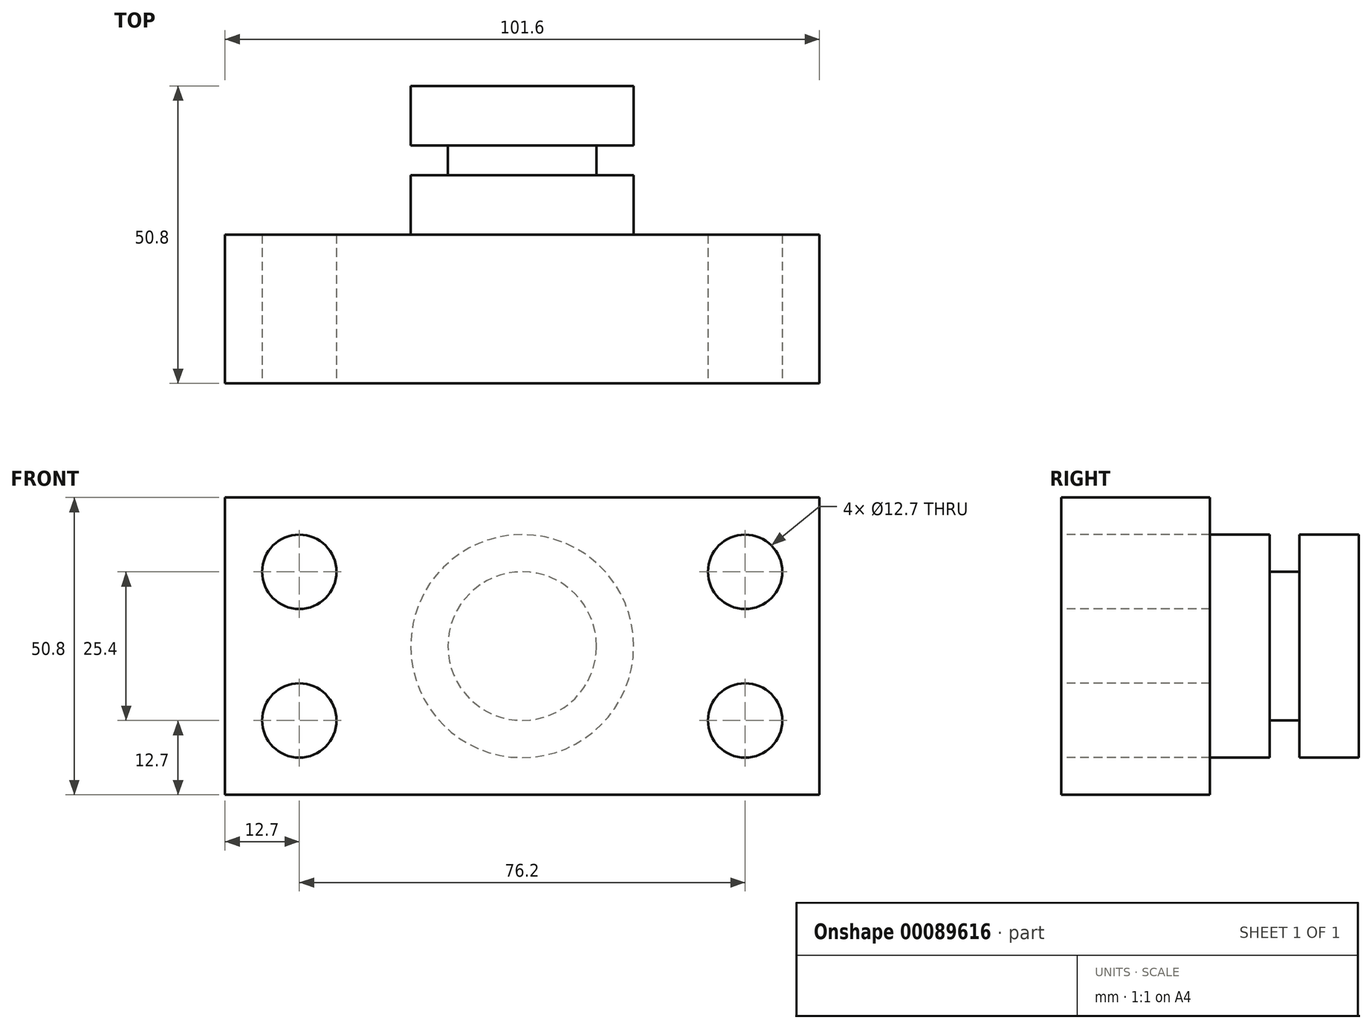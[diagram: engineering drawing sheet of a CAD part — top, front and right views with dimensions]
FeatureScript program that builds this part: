
annotation { "Feature Type Name" : "Feature", "Feature Type Description" : "" }
export const myFeature = defineFeature(function(context is Context, id is Id, definition is map)
    precondition{}
    {
        {
            var Q0;
            Q0=qCreatedBy(makeId("Front.planeOp"),FACE);
            var sketch = newSketch(context, id + "F0", { "sketchPlane" : qUnion([Q0])});
            skLineSegment(sketch, "E0", {"start": v(-50.8, 25.4) * mm, "end": v(50.8, 25.4) * mm});
            skLineSegment(sketch, "E1", {"start": v(50.8, 25.4) * mm, "end": v(50.8, -25.4) * mm});
            skLineSegment(sketch, "E2", {"start": v(50.8, -25.4) * mm, "end": v(-50.8, -25.4) * mm});
            skLineSegment(sketch, "E3", {"start": v(-50.8, -25.4) * mm, "end": v(-50.8, 25.4) * mm});
            skSolve(sketch);
        }
        {
            var Q0;
            Q0=makeQuery(id+"F0.imprint","IMPRINT",FACE,{"disambiguationData":[TD([[makeQuery(id+"F0.imprint","IMPRINT",EDGE,{"derivedFrom":sQuery(id+"F0.wireOp",EDGE,"E0")}),-1.0]])]});
            extrude(context, id + "F1", {"entities" : qUnion([Q0]), "depth" : 25.4 * mm});
        }
        {
            var Q0;
            Q0=makeQuery(id+"F1.opExtrude","CAP_FACE",FACE,{"disambiguationData":[OSD([sQuery(id+"F0.wireOp",EDGE,"E0"),sQuery(id+"F0.wireOp",EDGE,"E1"),sQuery(id+"F0.wireOp",EDGE,"E2"),sQuery(id+"F0.wireOp",EDGE,"E3")])],"isStart":false});
            var sketch = newSketch(context, id + "F2", { "sketchPlane" : qUnion([Q0])});
            skCircle(sketch, "E4", {"center": v(-38.1, 12.7) * mm, "radius": 6.35 * mm});
            skCircle(sketch, "E5", {"center": v(-38.1, -12.7) * mm, "radius": 6.35 * mm});
            skLineSegment(sketch, "E6", {"start": v(0, 34.69) * mm, "end": v(0, -31.44) * mm, "construction": true});
            skPoint(sketch, "E6.endSnap0", {"position": v(0, -25.4) * mm});
            skCircle(sketch, "E7.MirrorC", {"center": v(38.1, -12.7) * mm, "radius": 6.35 * mm});
            skCircle(sketch, "E8.MirrorC", {"center": v(38.1, 12.7) * mm, "radius": 6.35 * mm});
            skSolve(sketch);
        }
        {
            var Q0;
            Q0 = qSketchRegion(id + "F2", true);
            extrude(context, id + "F3", {"entities" : qUnion([Q0]), "operationType" : NewBodyOperationType.REMOVE, "endBound" : BoundingType.THROUGH_ALL, "oppositeDirection" : true, "depth" : 25.4 * mm});
        }
        {
            var Q0;
            Q0=qCreatedBy(makeId("Top.planeOp"),FACE);
            var sketch = newSketch(context, id + "F4", { "sketchPlane" : qUnion([Q0])});
            skLineSegment(sketch, "E9", {"start": v(-19.05, 0) * mm, "end": v(0, 0) * mm});
            skLineSegment(sketch, "E10", {"start": v(0, 0) * mm, "end": v(0, 25.4) * mm});
            skLineSegment(sketch, "E11", {"start": v(0, 25.4) * mm, "end": v(-19.05, 25.4) * mm});
            skLineSegment(sketch, "E12", {"start": v(-19.05, 25.4) * mm, "end": v(-19.05, 0) * mm});
            skLineSegment(sketch, "E13", {"start": v(0, 50.58) * mm, "end": v(0, -41.33) * mm});
            skSolve(sketch);
        }
        {
            var Q0;
            Q0 = qSketchRegion(id + "F4", true);
            var Q1;
            Q1=sQuery(id+"F4.wireOp",EDGE,"E13");
            revolve(context, id + "F5", {"operationType" : NewBodyOperationType.ADD, "entities" : qUnion([Q0]), "axis" : qUnion([Q1]), "revolveType" : RevolveType.FULL});
        }
        {
            var Q0;
            Q0=qCreatedBy(makeId("Top.planeOp"),FACE);
            var sketch = newSketch(context, id + "F6", { "sketchPlane" : qUnion([Q0])});
            skLineSegment(sketch, "E14.bottom", {"start": v(-19.05, 15.24) * mm, "end": v(-12.7, 15.24) * mm});
            skLineSegment(sketch, "E14.top", {"start": v(-19.05, 10.16) * mm, "end": v(-12.7, 10.16) * mm});
            skLineSegment(sketch, "E14.left", {"start": v(-19.05, 15.24) * mm, "end": v(-19.05, 10.16) * mm});
            skLineSegment(sketch, "E14.right", {"start": v(-12.7, 15.24) * mm, "end": v(-12.7, 10.16) * mm});
            skLineSegment(sketch, "E15", {"start": v(0, 0) * mm, "end": v(-19.05, 0) * mm});
            skLineSegment(sketch, "E16", {"start": v(0, 0) * mm, "end": v(0, 26.35) * mm});
            skSolve(sketch);
        }
        {
            var Q0;
            Q0 = qSketchRegion(id + "F6", true);
            var Q1;
            Q1=sQuery(id+"F6.wireOp",EDGE,"E16");
            revolve(context, id + "F7", {"operationType" : NewBodyOperationType.REMOVE, "entities" : qUnion([Q0]), "axis" : qUnion([Q1]), "revolveType" : RevolveType.FULL, "oppositeDirection" : true});
        }
    });
